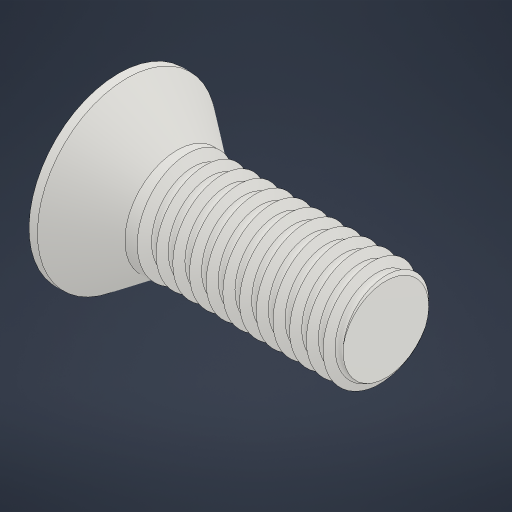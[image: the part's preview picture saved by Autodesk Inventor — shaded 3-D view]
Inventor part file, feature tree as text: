
AUTODESK INVENTOR PART (.ipt)
format: ipt  version: 2024 (Build 280153000, 153)  size: 559,104 bytes
history: native  units: mm
features: sketch x7, other x3, revolve x3, extrude x3, chamfer x2
ambient origin geometry x8: Origin, YZ Plane, XZ Plane, XY Plane, X Axis, Y Axis, Z Axis, Center Point
bodies: Body1 (feature_tree)
feature tree (18):
  other  "솔리드1"
  revolve  "회전1"
  other  "코일2"
  extrude  "돌출2"  Depth=2.8mm
  revolve  "회전2"
  sketch  "스케치9"
  extrude  "돌출3"  Depth=10.0mm
  revolve  "회전3"
  chamfer  "모따기1"  Distance=9.6mm
  chamfer  "모따기2"  Distance=5.0mm
  extrude  "돌출4"  TaperAngle=90.0deg  [1 undecoded]
  sketch  "스케치1"
  sketch  "스케치3"
  sketch  "스케치7"
  sketch  "스케치8"
  sketch  "스케치11"
  sketch  "스케치12"
  other  "Finish1"
note: 1 required parameter value undecoded (feature->parameter linkage not recoverable at this tier; creation-order binding heuristic only, values carry confidence <= 0.55)
